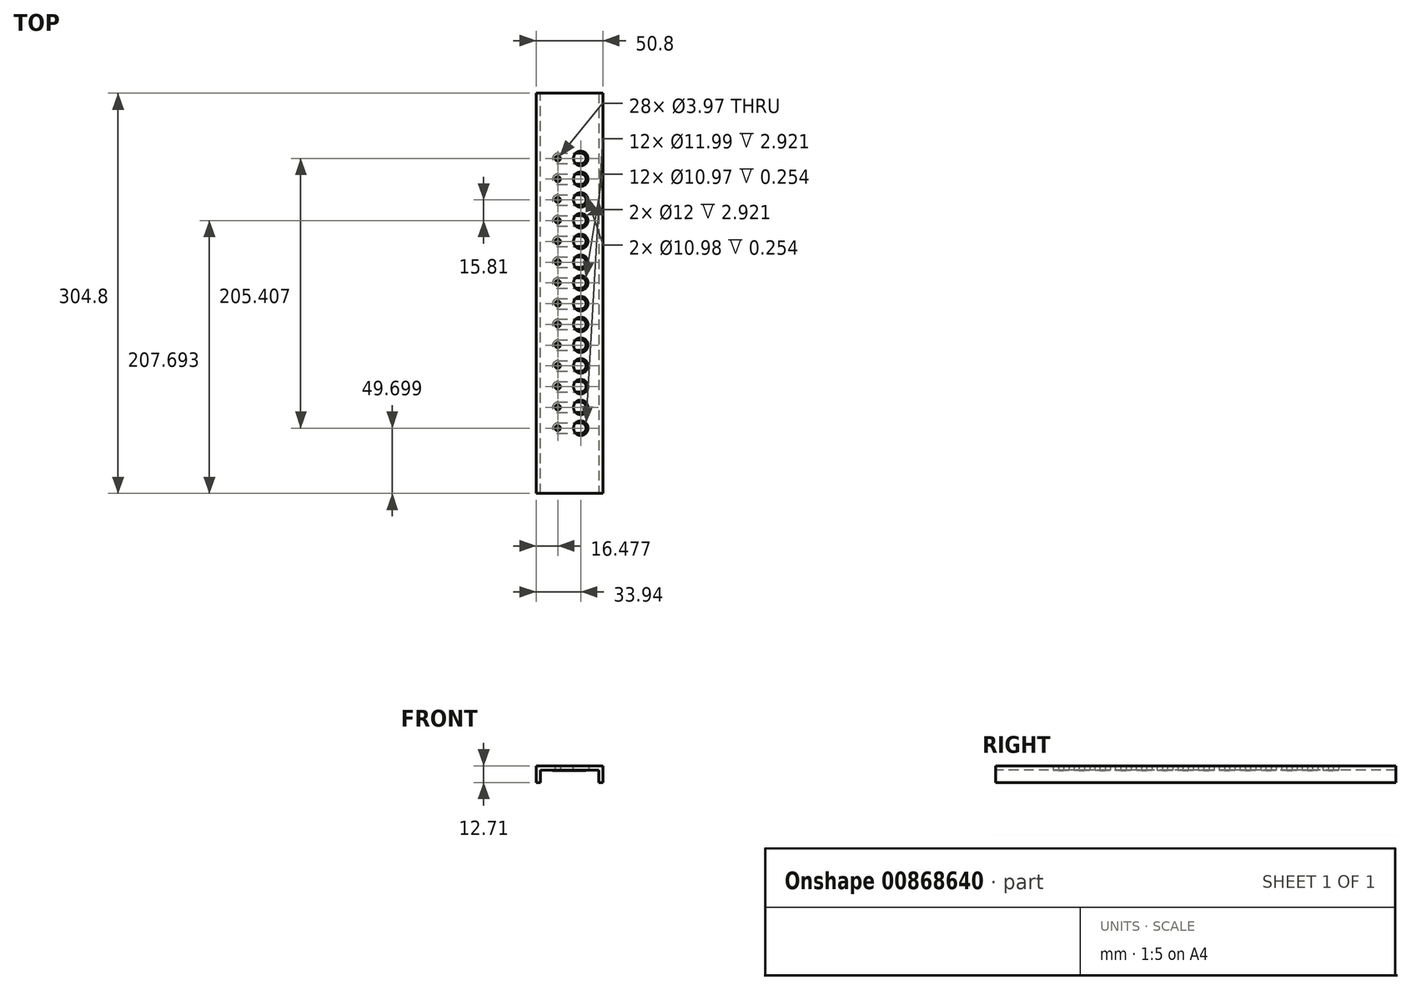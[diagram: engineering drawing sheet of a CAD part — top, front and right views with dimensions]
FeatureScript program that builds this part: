
annotation { "Feature Type Name" : "Feature", "Feature Type Description" : "" }
export const myFeature = defineFeature(function(context is Context, id is Id, definition is map)
    precondition{}
    {
        {
            var Q0;
            Q0=qCreatedBy(makeId("Top.planeOp"),FACE);
            var sketch = newSketch(context, id + "F0", { "sketchPlane" : qUnion([Q0])});
            skLineSegment(sketch, "E0.bottom", {"start": v(0, 0) * mm, "end": v(50.8, 0) * mm});
            skLineSegment(sketch, "E0.top", {"start": v(0, -304.8) * mm, "end": v(50.8, -304.8) * mm});
            skLineSegment(sketch, "E0.left", {"start": v(0, 0) * mm, "end": v(0, -304.8) * mm});
            skLineSegment(sketch, "E0.right", {"start": v(50.8, 0) * mm, "end": v(50.8, -304.8) * mm});
            skCircle(sketch, "E1", {"center": v(33.94, -81.3) * mm, "radius": 6 * mm});
            skLineSegment(sketch, "E2", {"start": v(33.94, 0) * mm, "end": v(33.94, -304.8) * mm, "construction": true});
            skCircle(sketch, "E3", {"center": v(33.94, -97.1) * mm, "radius": 6 * mm});
            skCircle(sketch, "E4", {"center": v(33.94, -112.91) * mm, "radius": 6 * mm});
            skCircle(sketch, "E5", {"center": v(33.94, -128.71) * mm, "radius": 6 * mm});
            skCircle(sketch, "E6", {"center": v(33.94, -144.5) * mm, "radius": 6 * mm});
            skCircle(sketch, "E7", {"center": v(33.94, -160.3) * mm, "radius": 6 * mm});
            skCircle(sketch, "E8", {"center": v(33.94, -176.1) * mm, "radius": 6 * mm});
            skCircle(sketch, "E9", {"center": v(33.94, -191.9) * mm, "radius": 6 * mm});
            skCircle(sketch, "E10", {"center": v(33.94, -207.7) * mm, "radius": 6 * mm});
            skLineSegment(sketch, "E11", {"start": v(47.63, 0) * mm, "end": v(47.63, -304.8) * mm});
            skLineSegment(sketch, "E12", {"start": v(3.18, -304.8) * mm, "end": v(3.18, 0) * mm});
            skCircle(sketch, "E13", {"center": v(33.94, -223.5) * mm, "radius": 6 * mm});
            skLineSegment(sketch, "E14", {"start": v(33.94, -223.5) * mm, "end": v(33.94, -286.7) * mm, "construction": true});
            skLineSegment(sketch, "E15", {"start": v(33.94, -255.1) * mm, "end": v(33.94, -81.3) * mm});
            skLineSegment(sketch, "E16", {"start": v(0, -152.4) * mm, "end": v(306.37, -152.4) * mm, "construction": true});
            skCircle(sketch, "E17", {"center": v(33.94, -239.3) * mm, "radius": 6 * mm});
            skCircle(sketch, "E18", {"center": v(33.94, -255.1) * mm, "radius": 6 * mm});
            skCircle(sketch, "E19", {"center": v(33.94, -65.5) * mm, "radius": 6 * mm});
            skCircle(sketch, "E20", {"center": v(33.94, -49.7) * mm, "radius": 6 * mm});
            skLineSegment(sketch, "E21", {"start": v(10.36, 0) * mm, "end": v(10.36, -40) * mm, "construction": true});
            skSolve(sketch);
        }
        {
            var Q0;
            Q0=makeQuery(id+"F0.imprint","IMPRINT",FACE,{"disambiguationData":[TD([[makeQuery(id+"F0.imprint","IMPRINT",EDGE,{"derivedFrom":sQuery(id+"F0.wireOp",EDGE,"E1")}),-1.0]])]});
            var Q1;
            {var subQ0=sQuery(id+"F0.wireOp",EDGE,"E0.right");Q1=makeQuery(id+"F0.imprint","IMPRINT",FACE,{"disambiguationData":[TD([[makeQuery(id+"F0.imprint","IMPRINT",EDGE,{"derivedFrom":subQ0}),-1.0]])]});}
            var Q2;
            {var subQ0=sQuery(id+"F0.wireOp",EDGE,"E0.left");Q2=makeQuery(id+"F0.imprint","IMPRINT",FACE,{"disambiguationData":[TD([[makeQuery(id+"F0.imprint","IMPRINT",EDGE,{"derivedFrom":subQ0}),1.0]])]});}
            extrude(context, id + "F1", {"entities" : qUnion([Q0, Q1, Q2]), "depth" : 2.92 * mm, "offsetDistance" : 25.4 * mm});
        }
        {
            var Q0;
            {var subQ0=sQuery(id+"F0.wireOp",EDGE,"E0.left");Q0=makeQuery(id+"F0.imprint","IMPRINT",FACE,{"disambiguationData":[TD([[makeQuery(id+"F0.imprint","IMPRINT",EDGE,{"derivedFrom":subQ0}),1.0]])]});}
            var Q1;
            {var subQ0=sQuery(id+"F0.wireOp",EDGE,"E0.right");Q1=makeQuery(id+"F0.imprint","IMPRINT",FACE,{"disambiguationData":[TD([[makeQuery(id+"F0.imprint","IMPRINT",EDGE,{"derivedFrom":subQ0}),-1.0]])]});}
            extrude(context, id + "F2", {"entities" : qUnion([Q0, Q1]), "operationType" : NewBodyOperationType.ADD, "oppositeDirection" : true, "depth" : 9.52 * mm, "offsetDistance" : 25.4 * mm});
        }
        {
            var Q0;
            Q0=makeQuery(id+"F1.opExtrude","CAP_FACE",FACE,{"disambiguationData":[OSD([sQuery(id+"F0.wireOp",EDGE,"E0.bottom"),sQuery(id+"F0.wireOp",EDGE,"E0.top"),sQuery(id+"F0.wireOp",EDGE,"E0.left"),sQuery(id+"F0.wireOp",EDGE,"E0.right"),sQuery(id+"F0.wireOp",EDGE,"E1"),sQuery(id+"F0.wireOp",EDGE,"E3"),sQuery(id+"F0.wireOp",EDGE,"E4"),sQuery(id+"F0.wireOp",EDGE,"E5"),sQuery(id+"F0.wireOp",EDGE,"E6"),sQuery(id+"F0.wireOp",EDGE,"E7"),sQuery(id+"F0.wireOp",EDGE,"E8"),sQuery(id+"F0.wireOp",EDGE,"E9"),sQuery(id+"F0.wireOp",EDGE,"E10")])],"isStart":false});
            var sketch = newSketch(context, id + "F3", { "sketchPlane" : qUnion([Q0])});
            skCircle(sketch, "E22", {"center": v(33.94, -81.3) * mm, "radius": 5.5 * mm});
            skCircle(sketch, "E23", {"center": v(33.94, -97.1) * mm, "radius": 5.5 * mm});
            skCircle(sketch, "E24", {"center": v(33.94, -128.71) * mm, "radius": 5.49 * mm});
            skCircle(sketch, "E25", {"center": v(33.94, -160.3) * mm, "radius": 5.49 * mm});
            skCircle(sketch, "E26", {"center": v(33.94, -112.91) * mm, "radius": 5.49 * mm});
            skCircle(sketch, "E27", {"center": v(33.94, -144.5) * mm, "radius": 5.49 * mm});
            skCircle(sketch, "E28", {"center": v(33.94, -176.1) * mm, "radius": 5.49 * mm});
            skCircle(sketch, "E29", {"center": v(33.94, -207.7) * mm, "radius": 5.49 * mm});
            skCircle(sketch, "E30", {"center": v(33.94, -191.9) * mm, "radius": 5.49 * mm});
            skCircle(sketch, "E31", {"center": v(33.94, -49.7) * mm, "radius": 5.49 * mm});
            skCircle(sketch, "E32", {"center": v(33.94, -65.5) * mm, "radius": 5.49 * mm});
            skCircle(sketch, "E33", {"center": v(33.94, -223.5) * mm, "radius": 5.49 * mm});
            skCircle(sketch, "E34", {"center": v(33.94, -239.3) * mm, "radius": 5.49 * mm});
            skCircle(sketch, "E35", {"center": v(33.94, -255.1) * mm, "radius": 5.49 * mm});
            skSolve(sketch);
        }
        {
            var Q0;
            Q0=makeQuery(id+"F3.imprint","IMPRINT",FACE,{"disambiguationData":[TD([[makeQuery(id+"F3.imprint","IMPRINT",EDGE,{"derivedFrom":sQuery(id+"F3.wireOp",EDGE,"E35")}),-1.0]])]});
            var Q1;
            Q1=makeQuery(id+"F3.imprint","IMPRINT",FACE,{"disambiguationData":[TD([[makeQuery(id+"F3.imprint","IMPRINT",EDGE,{"derivedFrom":sQuery(id+"F3.wireOp",EDGE,"E34")}),-1.0]])]});
            var Q2;
            Q2=makeQuery(id+"F3.imprint","IMPRINT",FACE,{"disambiguationData":[TD([[makeQuery(id+"F3.imprint","IMPRINT",EDGE,{"derivedFrom":sQuery(id+"F3.wireOp",EDGE,"E29")}),-1.0]])]});
            var Q3;
            Q3=makeQuery(id+"F3.imprint","IMPRINT",FACE,{"disambiguationData":[TD([[makeQuery(id+"F3.imprint","IMPRINT",EDGE,{"derivedFrom":makeQuery(id+"F1.opExtrude","CAP_EDGE",EDGE,{"disambiguationData":[OSD([sQuery(id+"F0.wireOp",EDGE,"E0.bottom")])],"isStart":false})}),-1.0]])]});
            var Q4;
            Q4=makeQuery(id+"F3.imprint","IMPRINT",FACE,{"disambiguationData":[TD([[makeQuery(id+"F3.imprint","IMPRINT",EDGE,{"derivedFrom":sQuery(id+"F3.wireOp",EDGE,"E30")}),-1.0]])]});
            var Q5;
            Q5=makeQuery(id+"F3.imprint","IMPRINT",FACE,{"disambiguationData":[TD([[makeQuery(id+"F3.imprint","IMPRINT",EDGE,{"derivedFrom":sQuery(id+"F3.wireOp",EDGE,"E28")}),-1.0]])]});
            var Q6;
            Q6=makeQuery(id+"F3.imprint","IMPRINT",FACE,{"disambiguationData":[TD([[makeQuery(id+"F3.imprint","IMPRINT",EDGE,{"derivedFrom":sQuery(id+"F3.wireOp",EDGE,"E25")}),-1.0]])]});
            var Q7;
            Q7=makeQuery(id+"F3.imprint","IMPRINT",FACE,{"disambiguationData":[TD([[makeQuery(id+"F3.imprint","IMPRINT",EDGE,{"derivedFrom":sQuery(id+"F3.wireOp",EDGE,"E27")}),-1.0]])]});
            var Q8;
            Q8=makeQuery(id+"F3.imprint","IMPRINT",FACE,{"disambiguationData":[TD([[makeQuery(id+"F3.imprint","IMPRINT",EDGE,{"derivedFrom":sQuery(id+"F3.wireOp",EDGE,"E24")}),-1.0]])]});
            var Q9;
            Q9=makeQuery(id+"F3.imprint","IMPRINT",FACE,{"disambiguationData":[TD([[makeQuery(id+"F3.imprint","IMPRINT",EDGE,{"derivedFrom":sQuery(id+"F3.wireOp",EDGE,"E26")}),-1.0]])]});
            var Q10;
            Q10=makeQuery(id+"F3.imprint","IMPRINT",FACE,{"disambiguationData":[TD([[makeQuery(id+"F3.imprint","IMPRINT",EDGE,{"derivedFrom":sQuery(id+"F3.wireOp",EDGE,"E33")}),-1.0]])]});
            var Q11;
            Q11=makeQuery(id+"F3.imprint","IMPRINT",FACE,{"disambiguationData":[TD([[makeQuery(id+"F3.imprint","IMPRINT",EDGE,{"derivedFrom":sQuery(id+"F3.wireOp",EDGE,"E22")}),-1.0]])]});
            var Q12;
            Q12=makeQuery(id+"F3.imprint","IMPRINT",FACE,{"disambiguationData":[TD([[makeQuery(id+"F3.imprint","IMPRINT",EDGE,{"derivedFrom":sQuery(id+"F3.wireOp",EDGE,"E31")}),-1.0]])]});
            var Q13;
            Q13=makeQuery(id+"F3.imprint","IMPRINT",FACE,{"disambiguationData":[TD([[makeQuery(id+"F3.imprint","IMPRINT",EDGE,{"derivedFrom":sQuery(id+"F3.wireOp",EDGE,"E23")}),-1.0]])]});
            var Q14;
            Q14=makeQuery(id+"F3.imprint","IMPRINT",FACE,{"disambiguationData":[TD([[makeQuery(id+"F3.imprint","IMPRINT",EDGE,{"derivedFrom":sQuery(id+"F3.wireOp",EDGE,"E32")}),-1.0]])]});
            extrude(context, id + "F4", {"entities" : qUnion([Q0, Q1, Q2, Q3, Q4, Q5, Q6, Q7, Q8, Q9, Q10, Q11, Q12, Q13, Q14]), "operationType" : NewBodyOperationType.ADD, "depth" : 0.25 * mm, "offsetDistance" : 25.4 * mm});
        }
        {
            var Q0;
            Q0=makeQuery(id+"F0.imprint","IMPRINT",FACE,{"disambiguationData":[TD([[makeQuery(id+"F0.imprint","IMPRINT",EDGE,{"derivedFrom":sQuery(id+"F0.wireOp",EDGE,"E1")}),-1.0]])]});
            var sketch = newSketch(context, id + "F5", { "sketchPlane" : qUnion([Q0])});
            skLineSegment(sketch, "E36.bottom", {"start": v(16.48, -227.47) * mm, "end": v(33.94, -227.47) * mm});
            skLineSegment(sketch, "E36.top", {"start": v(16.48, -219.53) * mm, "end": v(33.94, -219.53) * mm});
            skArc(sketch, "E37", {"start": v(33.94, -227.47) * mm, "mid": v(37.9, -223.5) * mm, "end": v(33.94, -219.53) * mm});
            skArc(sketch, "E38", {"start": v(16.48, -227.47) * mm, "mid": v(12.5, -223.5) * mm, "end": v(16.48, -219.53) * mm});
            skCircle(sketch, "E39", {"center": v(16.48, -223.5) * mm, "radius": 1.98 * mm});
            skLineSegment(sketch, "E40.bottom", {"start": v(16.48, -211.67) * mm, "end": v(33.94, -211.67) * mm});
            skLineSegment(sketch, "E40.top", {"start": v(16.48, -203.74) * mm, "end": v(33.94, -203.74) * mm});
            skArc(sketch, "E41", {"start": v(33.94, -211.67) * mm, "mid": v(37.9, -207.7) * mm, "end": v(33.94, -203.74) * mm});
            skArc(sketch, "E42", {"start": v(16.48, -211.67) * mm, "mid": v(12.5, -207.7) * mm, "end": v(16.48, -203.74) * mm});
            skCircle(sketch, "E43", {"center": v(16.48, -207.7) * mm, "radius": 1.98 * mm});
            skLineSegment(sketch, "E44.bottom", {"start": v(16.48, -195.87) * mm, "end": v(33.94, -195.87) * mm});
            skLineSegment(sketch, "E44.top", {"start": v(16.48, -187.94) * mm, "end": v(33.94, -187.94) * mm});
            skArc(sketch, "E45", {"start": v(33.94, -195.87) * mm, "mid": v(37.9, -191.9) * mm, "end": v(33.94, -187.94) * mm});
            skArc(sketch, "E46", {"start": v(16.48, -195.87) * mm, "mid": v(12.5, -191.9) * mm, "end": v(16.48, -187.94) * mm});
            skCircle(sketch, "E47", {"center": v(16.48, -191.9) * mm, "radius": 1.98 * mm});
            skLineSegment(sketch, "E48.bottom", {"start": v(16.48, -180.08) * mm, "end": v(33.94, -180.08) * mm});
            skLineSegment(sketch, "E48.top", {"start": v(16.48, -172.14) * mm, "end": v(33.94, -172.14) * mm});
            skArc(sketch, "E49", {"start": v(33.94, -180.08) * mm, "mid": v(37.9, -176.1) * mm, "end": v(33.94, -172.14) * mm});
            skArc(sketch, "E50", {"start": v(16.48, -180.08) * mm, "mid": v(12.5, -176.1) * mm, "end": v(16.48, -172.14) * mm});
            skCircle(sketch, "E51", {"center": v(16.48, -176.1) * mm, "radius": 1.98 * mm});
            skLineSegment(sketch, "E52.bottom", {"start": v(16.48, -164.28) * mm, "end": v(33.94, -164.28) * mm});
            skLineSegment(sketch, "E52.top", {"start": v(16.48, -156.34) * mm, "end": v(33.94, -156.34) * mm});
            skArc(sketch, "E53", {"start": v(33.94, -164.28) * mm, "mid": v(37.9, -160.3) * mm, "end": v(33.94, -156.34) * mm});
            skArc(sketch, "E54", {"start": v(16.48, -164.28) * mm, "mid": v(12.5, -160.3) * mm, "end": v(16.48, -156.34) * mm});
            skCircle(sketch, "E55", {"center": v(16.48, -160.3) * mm, "radius": 1.98 * mm});
            skLineSegment(sketch, "E56.bottom", {"start": v(16.48, -148.48) * mm, "end": v(33.94, -148.48) * mm});
            skLineSegment(sketch, "E56.top", {"start": v(16.48, -140.54) * mm, "end": v(33.94, -140.54) * mm});
            skArc(sketch, "E57", {"start": v(33.94, -148.48) * mm, "mid": v(37.9, -144.5) * mm, "end": v(33.94, -140.54) * mm});
            skArc(sketch, "E58", {"start": v(16.48, -148.48) * mm, "mid": v(12.5, -144.5) * mm, "end": v(16.48, -140.54) * mm});
            skCircle(sketch, "E59", {"center": v(16.48, -144.5) * mm, "radius": 1.98 * mm});
            skLineSegment(sketch, "E60.bottom", {"start": v(16.48, -132.68) * mm, "end": v(33.94, -132.68) * mm});
            skLineSegment(sketch, "E60.top", {"start": v(16.48, -124.74) * mm, "end": v(33.94, -124.74) * mm});
            skArc(sketch, "E61", {"start": v(33.94, -132.68) * mm, "mid": v(37.9, -128.71) * mm, "end": v(33.94, -124.74) * mm});
            skArc(sketch, "E62", {"start": v(16.48, -132.68) * mm, "mid": v(12.5, -128.71) * mm, "end": v(16.48, -124.74) * mm});
            skCircle(sketch, "E63", {"center": v(16.48, -128.71) * mm, "radius": 1.98 * mm});
            skLineSegment(sketch, "E64.bottom", {"start": v(16.48, -116.88) * mm, "end": v(33.94, -116.88) * mm});
            skLineSegment(sketch, "E64.top", {"start": v(16.48, -108.94) * mm, "end": v(33.94, -108.94) * mm});
            skArc(sketch, "E65", {"start": v(33.94, -116.88) * mm, "mid": v(37.9, -112.91) * mm, "end": v(33.94, -108.94) * mm});
            skArc(sketch, "E66", {"start": v(16.48, -116.88) * mm, "mid": v(12.5, -112.91) * mm, "end": v(16.48, -108.94) * mm});
            skCircle(sketch, "E67", {"center": v(16.48, -112.91) * mm, "radius": 1.98 * mm});
            skLineSegment(sketch, "E68.bottom", {"start": v(16.48, -101.08) * mm, "end": v(33.94, -101.08) * mm});
            skLineSegment(sketch, "E68.top", {"start": v(16.48, -93.14) * mm, "end": v(33.94, -93.14) * mm});
            skArc(sketch, "E69", {"start": v(33.94, -101.08) * mm, "mid": v(37.9, -97.1) * mm, "end": v(33.94, -93.14) * mm});
            skArc(sketch, "E70", {"start": v(16.48, -101.08) * mm, "mid": v(12.5, -97.1) * mm, "end": v(16.48, -93.14) * mm});
            skCircle(sketch, "E71", {"center": v(16.48, -97.1) * mm, "radius": 1.98 * mm});
            skLineSegment(sketch, "E72.bottom", {"start": v(16.48, -85.27) * mm, "end": v(33.94, -85.27) * mm});
            skLineSegment(sketch, "E72.top", {"start": v(16.48, -77.33) * mm, "end": v(33.94, -77.33) * mm});
            skArc(sketch, "E73", {"start": v(33.94, -85.27) * mm, "mid": v(37.9, -81.3) * mm, "end": v(33.94, -77.33) * mm});
            skArc(sketch, "E74", {"start": v(16.48, -85.27) * mm, "mid": v(12.5, -81.3) * mm, "end": v(16.48, -77.33) * mm});
            skCircle(sketch, "E75", {"center": v(16.48, -81.3) * mm, "radius": 1.98 * mm});
            skLineSegment(sketch, "E76.bottom", {"start": v(16.48, -69.46) * mm, "end": v(33.94, -69.46) * mm});
            skLineSegment(sketch, "E76.top", {"start": v(16.48, -61.52) * mm, "end": v(33.94, -61.52) * mm});
            skArc(sketch, "E77", {"start": v(33.94, -69.46) * mm, "mid": v(37.9, -65.5) * mm, "end": v(33.94, -61.52) * mm});
            skArc(sketch, "E78", {"start": v(16.48, -69.46) * mm, "mid": v(12.5, -65.5) * mm, "end": v(16.48, -61.52) * mm});
            skCircle(sketch, "E79", {"center": v(16.48, -65.5) * mm, "radius": 1.98 * mm});
            skLineSegment(sketch, "E80.bottom", {"start": v(16.48, -259.07) * mm, "end": v(33.94, -259.07) * mm});
            skLineSegment(sketch, "E80.top", {"start": v(16.48, -251.13) * mm, "end": v(33.94, -251.13) * mm});
            skArc(sketch, "E81", {"start": v(33.94, -259.07) * mm, "mid": v(37.9, -255.1) * mm, "end": v(33.94, -251.13) * mm});
            skArc(sketch, "E82", {"start": v(16.48, -259.07) * mm, "mid": v(12.5, -255.1) * mm, "end": v(16.48, -251.13) * mm});
            skCircle(sketch, "E83", {"center": v(16.48, -255.1) * mm, "radius": 1.98 * mm});
            skLineSegment(sketch, "E84.bottom", {"start": v(16.48, -243.27) * mm, "end": v(33.94, -243.27) * mm});
            skLineSegment(sketch, "E84.top", {"start": v(16.48, -235.33) * mm, "end": v(33.94, -235.33) * mm});
            skArc(sketch, "E85", {"start": v(33.94, -243.27) * mm, "mid": v(37.9, -239.3) * mm, "end": v(33.94, -235.33) * mm});
            skArc(sketch, "E86", {"start": v(16.48, -243.27) * mm, "mid": v(12.5, -239.3) * mm, "end": v(16.48, -235.33) * mm});
            skCircle(sketch, "E87", {"center": v(16.48, -239.3) * mm, "radius": 1.98 * mm});
            skLineSegment(sketch, "E88.bottom", {"start": v(16.48, -53.66) * mm, "end": v(33.94, -53.66) * mm});
            skLineSegment(sketch, "E88.top", {"start": v(16.48, -45.73) * mm, "end": v(33.94, -45.73) * mm});
            skArc(sketch, "E89", {"start": v(33.94, -53.66) * mm, "mid": v(37.9, -49.7) * mm, "end": v(33.94, -45.73) * mm});
            skArc(sketch, "E90", {"start": v(16.48, -53.66) * mm, "mid": v(12.5, -49.7) * mm, "end": v(16.48, -45.73) * mm});
            skCircle(sketch, "E91", {"center": v(16.48, -49.7) * mm, "radius": 1.98 * mm});
            skLineSegment(sketch, "E92", {"start": v(6.35, 0.95) * mm, "end": v(6.35, -306.7) * mm, "construction": true});
            skLineSegment(sketch, "E93", {"start": v(44.45, 0) * mm, "end": v(44.45, -305.86) * mm, "construction": true});
            skSolve(sketch);
        }
        {
            var Q0;
            Q0 = qSketchRegion(id + "F5", true);
            extrude(context, id + "F6", {"entities" : qUnion([Q0]), "oppositeDirection" : true, "depth" : 0.25 * mm, "offsetDistance" : 25.4 * mm});
        }
        {
            var Q0;
            Q0=makeQuery(id+"F5.imprint","IMPRINT",FACE,{"disambiguationData":[TD([[makeQuery(id+"F5.imprint","IMPRINT",EDGE,{"derivedFrom":sQuery(id+"F5.wireOp",EDGE,"E39")}),1.0]])]});
            var Q1;
            Q1=makeQuery(id+"F5.imprint","IMPRINT",FACE,{"disambiguationData":[TD([[makeQuery(id+"F5.imprint","IMPRINT",EDGE,{"derivedFrom":sQuery(id+"F5.wireOp",EDGE,"E43")}),1.0]])]});
            var Q2;
            Q2=makeQuery(id+"F5.imprint","IMPRINT",FACE,{"disambiguationData":[TD([[makeQuery(id+"F5.imprint","IMPRINT",EDGE,{"derivedFrom":sQuery(id+"F5.wireOp",EDGE,"E47")}),1.0]])]});
            var Q3;
            Q3=makeQuery(id+"F5.imprint","IMPRINT",FACE,{"disambiguationData":[TD([[makeQuery(id+"F5.imprint","IMPRINT",EDGE,{"derivedFrom":sQuery(id+"F5.wireOp",EDGE,"E51")}),1.0]])]});
            var Q4;
            Q4=makeQuery(id+"F5.imprint","IMPRINT",FACE,{"disambiguationData":[TD([[makeQuery(id+"F5.imprint","IMPRINT",EDGE,{"derivedFrom":sQuery(id+"F5.wireOp",EDGE,"E55")}),1.0]])]});
            var Q5;
            Q5=makeQuery(id+"F5.imprint","IMPRINT",FACE,{"disambiguationData":[TD([[makeQuery(id+"F5.imprint","IMPRINT",EDGE,{"derivedFrom":sQuery(id+"F5.wireOp",EDGE,"E59")}),1.0]])]});
            var Q6;
            Q6=makeQuery(id+"F5.imprint","IMPRINT",FACE,{"disambiguationData":[TD([[makeQuery(id+"F5.imprint","IMPRINT",EDGE,{"derivedFrom":sQuery(id+"F5.wireOp",EDGE,"E63")}),1.0]])]});
            var Q7;
            Q7=makeQuery(id+"F5.imprint","IMPRINT",FACE,{"disambiguationData":[TD([[makeQuery(id+"F5.imprint","IMPRINT",EDGE,{"derivedFrom":sQuery(id+"F5.wireOp",EDGE,"E67")}),1.0]])]});
            var Q8;
            Q8=makeQuery(id+"F5.imprint","IMPRINT",FACE,{"disambiguationData":[TD([[makeQuery(id+"F5.imprint","IMPRINT",EDGE,{"derivedFrom":sQuery(id+"F5.wireOp",EDGE,"E71")}),1.0]])]});
            var Q9;
            Q9=makeQuery(id+"F5.imprint","IMPRINT",FACE,{"disambiguationData":[TD([[makeQuery(id+"F5.imprint","IMPRINT",EDGE,{"derivedFrom":sQuery(id+"F5.wireOp",EDGE,"E75")}),1.0]])]});
            var Q10;
            Q10=makeQuery(id+"F5.imprint","IMPRINT",FACE,{"disambiguationData":[TD([[makeQuery(id+"F5.imprint","IMPRINT",EDGE,{"derivedFrom":sQuery(id+"F5.wireOp",EDGE,"E79")}),1.0]])]});
            var Q11;
            Q11=makeQuery(id+"F5.imprint","IMPRINT",FACE,{"disambiguationData":[TD([[makeQuery(id+"F5.imprint","IMPRINT",EDGE,{"derivedFrom":sQuery(id+"F5.wireOp",EDGE,"E91")}),1.0]])]});
            var Q12;
            Q12=makeQuery(id+"F5.imprint","IMPRINT",FACE,{"disambiguationData":[TD([[makeQuery(id+"F5.imprint","IMPRINT",EDGE,{"derivedFrom":sQuery(id+"F5.wireOp",EDGE,"E87")}),1.0]])]});
            var Q13;
            Q13=makeQuery(id+"F5.imprint","IMPRINT",FACE,{"disambiguationData":[TD([[makeQuery(id+"F5.imprint","IMPRINT",EDGE,{"derivedFrom":sQuery(id+"F5.wireOp",EDGE,"E83")}),1.0]])]});
            extrude(context, id + "F7", {"entities" : qUnion([Q0, Q1, Q2, Q3, Q4, Q5, Q6, Q7, Q8, Q9, Q10, Q11, Q12, Q13]), "operationType" : NewBodyOperationType.REMOVE, "endBound" : BoundingType.THROUGH_ALL, "depth" : 25.4 * mm, "offsetDistance" : 25.4 * mm});
        }
    });
